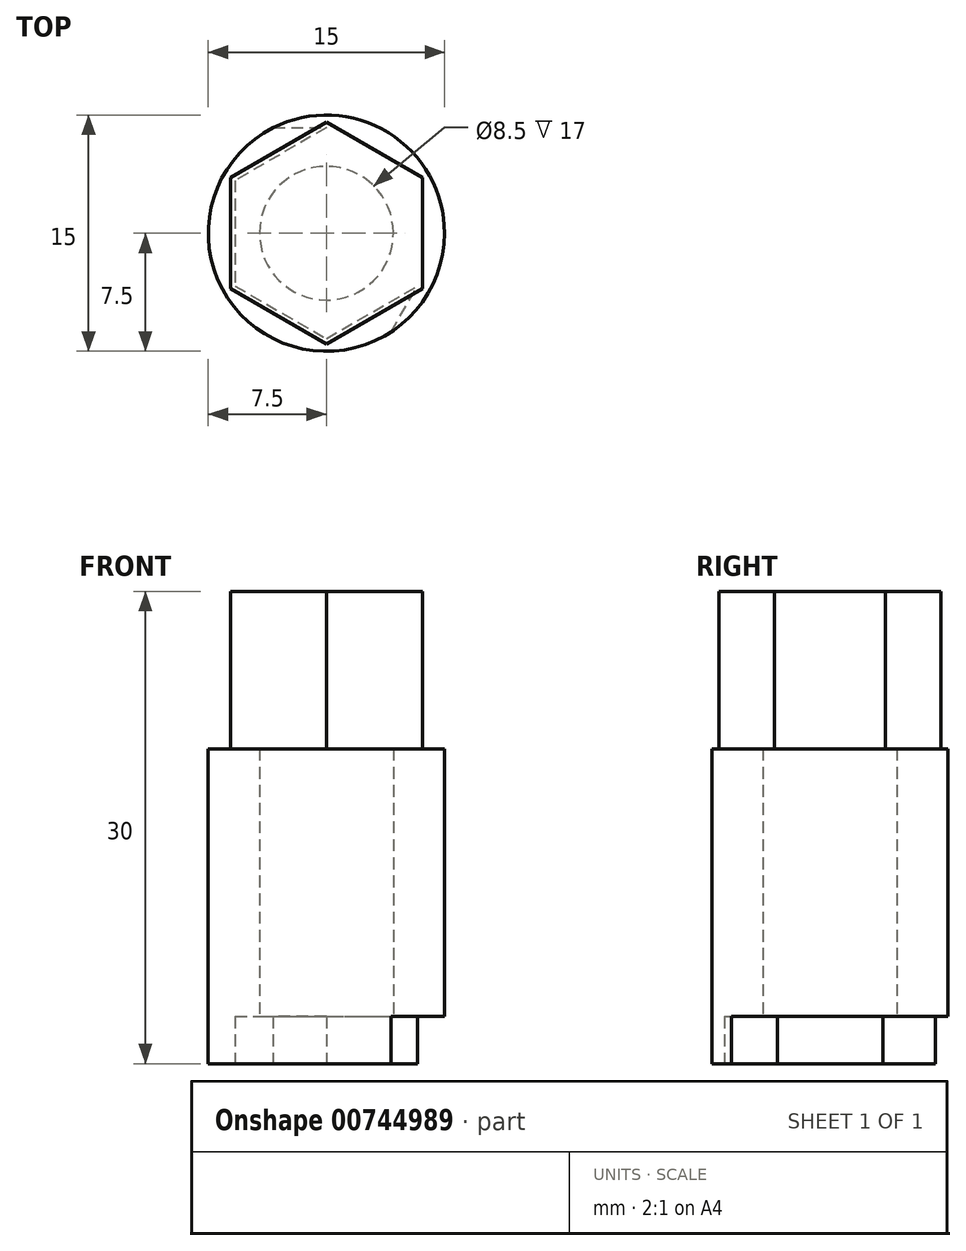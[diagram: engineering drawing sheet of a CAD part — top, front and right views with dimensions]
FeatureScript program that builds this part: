
annotation { "Feature Type Name" : "Feature", "Feature Type Description" : "" }
export const myFeature = defineFeature(function(context is Context, id is Id, definition is map)
    precondition{}
    {
        {
            var Q0;
            Q0=qCreatedBy(makeId("Top.planeOp"),FACE);
            var sketch = newSketch(context, id + "F0", { "sketchPlane" : qUnion([Q0])});
            skCircle(sketch, "E0", {"center": v(0, 0) * mm, "radius": 7.5 * mm});
            skSolve(sketch);
        }
        {
            var Q0;
            Q0=makeQuery(id+"F0.imprint","IMPRINT",FACE,{"disambiguationData":[TD([[makeQuery(id+"F0.imprint","IMPRINT",EDGE,{"derivedFrom":sQuery(id+"F0.wireOp",EDGE,"E0")}),1.0]])]});
            extrude(context, id + "F1", {"entities" : qUnion([Q0]), "depth" : 30 * mm, "offsetDistance" : 25 * mm});
        }
        {
            var Q0;
            Q0=makeQuery(id+"F1.opExtrude","CAP_FACE",FACE,{"disambiguationData":[OSD([sQuery(id+"F0.wireOp",EDGE,"E0")])],"isStart":true});
            var sketch = newSketch(context, id + "F2", { "sketchPlane" : qUnion([Q0])});
            skCircle(sketch, "E1", {"center": v(0, 0) * mm, "radius": 4.25 * mm});
            skSolve(sketch);
        }
        {
            var Q0;
            Q0=makeQuery(id+"F2.imprint","IMPRINT",FACE,{"disambiguationData":[TD([[makeQuery(id+"F2.imprint","IMPRINT",EDGE,{"derivedFrom":sQuery(id+"F2.wireOp",EDGE,"E1")}),1.0]])]});
            extrude(context, id + "F3", {"entities" : qUnion([Q0]), "operationType" : NewBodyOperationType.REMOVE, "oppositeDirection" : true, "depth" : 20 * mm, "offsetDistance" : 25 * mm});
        }
        {
            var Q0;
            Q0=makeQuery(id+"F1.opExtrude","CAP_FACE",FACE,{"disambiguationData":[OSD([sQuery(id+"F0.wireOp",EDGE,"E0")])],"isStart":true});
            var sketch = newSketch(context, id + "F4", { "sketchPlane" : qUnion([Q0])});
            skCircle(sketch, "E2.cCircle", {"center": v(0, 0) * mm, "radius": 5.8 * mm, "construction": true});
            skLineSegment(sketch, "E2.0", {"start": v(5.8, 3.35) * mm, "end": v(5.8, -3.35) * mm});
            skLineSegment(sketch, "E2.1", {"start": v(5.8, -3.35) * mm, "end": v(0, -6.7) * mm});
            skLineSegment(sketch, "E2.2", {"start": v(0, -6.7) * mm, "end": v(-5.8, -3.35) * mm});
            skLineSegment(sketch, "E2.3", {"start": v(-5.8, -3.35) * mm, "end": v(-5.8, 3.35) * mm});
            skLineSegment(sketch, "E2.4", {"start": v(-5.8, 3.35) * mm, "end": v(0, 6.7) * mm});
            skLineSegment(sketch, "E2.5", {"start": v(0, 6.7) * mm, "end": v(5.8, 3.35) * mm});
            skPoint(sketch, "E2.0.midPoint", {"position": v(5.8, 0) * mm});
            skSolve(sketch);
        }
        {
            var Q0;
            Q0=makeQuery(id+"F4.imprint","IMPRINT",FACE,{"disambiguationData":[TD([[makeQuery(id+"F4.imprint","IMPRINT",EDGE,{"derivedFrom":sQuery(id+"F4.wireOp",EDGE,"E2.0")}),-1.0]])]});
            extrude(context, id + "F5", {"entities" : qUnion([Q0]), "operationType" : NewBodyOperationType.REMOVE, "oppositeDirection" : true, "depth" : 3 * mm, "offsetDistance" : 25 * mm});
        }
        {
            var Q0;
            Q0=makeQuery(id+"F1.opExtrude","CAP_FACE",FACE,{"disambiguationData":[OSD([sQuery(id+"F0.wireOp",EDGE,"E0")])],"isStart":true});
            var sketch = newSketch(context, id + "F6", { "sketchPlane" : qUnion([Q0])});
            skCircle(sketch, "E3", {"center": v(0, 0) * mm, "radius": 6.5 * mm});
            skSolve(sketch);
        }
        {
            var Q0;
            Q0=makeQuery(id+"F1.opExtrude","CAP_FACE",FACE,{"disambiguationData":[OSD([sQuery(id+"F0.wireOp",EDGE,"E0")])],"isStart":false});
            var sketch = newSketch(context, id + "F7", { "sketchPlane" : qUnion([Q0])});
            skCircle(sketch, "E4.cCircle", {"center": v(0, 0) * mm, "radius": 6.1 * mm, "construction": true});
            skLineSegment(sketch, "E4.0", {"start": v(6.1, 3.52) * mm, "end": v(6.1, -3.52) * mm});
            skLineSegment(sketch, "E4.1", {"start": v(6.1, -3.52) * mm, "end": v(0, -7.04) * mm});
            skLineSegment(sketch, "E4.2", {"start": v(0, -7.04) * mm, "end": v(-6.1, -3.52) * mm});
            skLineSegment(sketch, "E4.3", {"start": v(-6.1, -3.52) * mm, "end": v(-6.1, 3.52) * mm});
            skLineSegment(sketch, "E4.4", {"start": v(-6.1, 3.52) * mm, "end": v(0, 7.04) * mm});
            skLineSegment(sketch, "E4.5", {"start": v(0, 7.04) * mm, "end": v(6.1, 3.52) * mm});
            skPoint(sketch, "E4.0.midPoint", {"position": v(6.1, 0) * mm});
            skSolve(sketch);
        }
        {
            var Q0;
            Q0=makeQuery(id+"F7.imprint","IMPRINT",FACE,{"disambiguationData":[TD([[makeQuery(id+"F7.imprint","IMPRINT",EDGE,{"derivedFrom":sQuery(id+"F7.wireOp",EDGE,"E4.0")}),1.0]])]});
            var Q1;
            {var subQ0=sQuery(id+"F7.wireOp",EDGE,"E4.5");var subQ1=makeQuery(id+"F1.opExtrude","CAP_EDGE",EDGE,{"disambiguationData":[OSD([sQuery(id+"F0.wireOp",EDGE,"E0")])],"isStart":false});var subQ2=makeQuery(id+"F7.imprint","INTERSECT",VERTEX,{"disambiguationData":[OD(0.0)],"derivedFrom":[subQ1,subQ0]});Q1=makeQuery(id+"F7.imprint","IMPRINT",FACE,{"disambiguationData":[TD([[makeQuery(id+"F7.imprint","IMPRINT",EDGE,{"disambiguationData":[TD([[subQ2,-1.0]])],"derivedFrom":subQ0}),1.0]])]});}
            var Q2;
            {var subQ0=sQuery(id+"F7.wireOp",EDGE,"E4.4");var subQ1=makeQuery(id+"F1.opExtrude","CAP_EDGE",EDGE,{"disambiguationData":[OSD([sQuery(id+"F0.wireOp",EDGE,"E0")])],"isStart":false});var subQ2=makeQuery(id+"F7.imprint","INTERSECT",VERTEX,{"disambiguationData":[OD(0.0)],"derivedFrom":[subQ1,subQ0]});Q2=makeQuery(id+"F7.imprint","IMPRINT",FACE,{"disambiguationData":[TD([[makeQuery(id+"F7.imprint","IMPRINT",EDGE,{"disambiguationData":[TD([[subQ2,-1.0]])],"derivedFrom":subQ0}),1.0]])]});}
            var Q3;
            {var subQ0=sQuery(id+"F7.wireOp",EDGE,"E4.3");var subQ1=makeQuery(id+"F1.opExtrude","CAP_EDGE",EDGE,{"disambiguationData":[OSD([sQuery(id+"F0.wireOp",EDGE,"E0")])],"isStart":false});var subQ2=makeQuery(id+"F7.imprint","INTERSECT",VERTEX,{"disambiguationData":[OD(0.0)],"derivedFrom":[subQ1,subQ0]});Q3=makeQuery(id+"F7.imprint","IMPRINT",FACE,{"disambiguationData":[TD([[makeQuery(id+"F7.imprint","IMPRINT",EDGE,{"disambiguationData":[TD([[subQ2,-1.0]])],"derivedFrom":subQ0}),1.0]])]});}
            var Q4;
            {var subQ0=sQuery(id+"F7.wireOp",EDGE,"E4.2");var subQ1=makeQuery(id+"F1.opExtrude","CAP_EDGE",EDGE,{"disambiguationData":[OSD([sQuery(id+"F0.wireOp",EDGE,"E0")])],"isStart":false});var subQ2=makeQuery(id+"F7.imprint","INTERSECT",VERTEX,{"disambiguationData":[OD(0.0)],"derivedFrom":[subQ1,subQ0]});Q4=makeQuery(id+"F7.imprint","IMPRINT",FACE,{"disambiguationData":[TD([[makeQuery(id+"F7.imprint","IMPRINT",EDGE,{"disambiguationData":[TD([[subQ2,-1.0]])],"derivedFrom":subQ0}),1.0]])]});}
            var Q5;
            {var subQ0=sQuery(id+"F7.wireOp",EDGE,"E4.1");var subQ1=makeQuery(id+"F1.opExtrude","CAP_EDGE",EDGE,{"disambiguationData":[OSD([sQuery(id+"F0.wireOp",EDGE,"E0")])],"isStart":false});var subQ2=makeQuery(id+"F7.imprint","INTERSECT",VERTEX,{"disambiguationData":[OD(0.0)],"derivedFrom":[subQ1,subQ0]});Q5=makeQuery(id+"F7.imprint","IMPRINT",FACE,{"disambiguationData":[TD([[makeQuery(id+"F7.imprint","IMPRINT",EDGE,{"disambiguationData":[TD([[subQ2,-1.0]])],"derivedFrom":subQ0}),1.0]])]});}
            extrude(context, id + "F8", {"entities" : qUnion([Q0, Q1, Q2, Q3, Q4, Q5]), "operationType" : NewBodyOperationType.REMOVE, "oppositeDirection" : true, "depth" : 10 * mm, "offsetDistance" : 25 * mm});
        }
        {
            var Q0;
            Q0=makeQuery(id+"F1.opExtrude","CAP_FACE",FACE,{"disambiguationData":[OSD([sQuery(id+"F0.wireOp",EDGE,"E0")])],"isStart":true});
            var sketch = newSketch(context, id + "F9", { "sketchPlane" : qUnion([Q0])});
            skLineSegment(sketch, "E5.0.0", {"start": v(5.8, 3.35) * mm, "end": v(0, 6.7) * mm});
            skLineSegment(sketch, "E5.0.1", {"start": v(0, 6.7) * mm, "end": v(-5.8, 3.35) * mm});
            skLineSegment(sketch, "E5.0.2", {"start": v(-5.8, 3.35) * mm, "end": v(-5.8, -3.35) * mm});
            skLineSegment(sketch, "E5.0.3", {"start": v(-5.8, -3.35) * mm, "end": v(0, -6.7) * mm});
            skLineSegment(sketch, "E5.0.4", {"start": v(0, -6.7) * mm, "end": v(5.8, -3.35) * mm});
            skLineSegment(sketch, "E5.0.5", {"start": v(5.8, -3.35) * mm, "end": v(5.8, 3.35) * mm});
            skCircle(sketch, "E6.0", {"center": v(0, 0) * mm, "radius": 4.25 * mm});
            skCircle(sketch, "E7.0", {"center": v(0, 0) * mm, "radius": 7.5 * mm});
            skLineSegment(sketch, "E8", {"start": v(4.11, 6.27) * mm, "end": v(5.8, 3.35) * mm});
            skPoint(sketch, "E9", {"position": v(5.8, 3.35) * mm});
            skLineSegment(sketch, "E10", {"start": v(-3.38, -6.7) * mm, "end": v(0, -6.7) * mm});
            skPoint(sketch, "E11", {"position": v(0, -6.7) * mm});
            skSolve(sketch);
        }
        {
            var Q0;
            Q0=makeQuery(id+"F9.imprint","IMPRINT",FACE,{"disambiguationData":[TD([[makeQuery(id+"F9.imprint","IMPRINT",EDGE,{"derivedFrom":sQuery(id+"F9.wireOp",EDGE,"E5.0.4")}),1.0]])]});
            var Q1;
            Q1=makeQuery(id+"F5.boolean.opBoolean","COPY",FACE,{"derivedFrom":makeQuery(id+"F5.opExtrude","CAP_FACE",FACE,{"disambiguationData":[OSD([sQuery(id+"F2.wireOp",EDGE,"E1"),sQuery(id+"F4.wireOp",EDGE,"E2.0"),sQuery(id+"F4.wireOp",EDGE,"E2.1"),sQuery(id+"F4.wireOp",EDGE,"E2.2"),sQuery(id+"F4.wireOp",EDGE,"E2.3"),sQuery(id+"F4.wireOp",EDGE,"E2.4"),sQuery(id+"F4.wireOp",EDGE,"E2.5")])],"isStart":false})});
            extrude(context, id + "F10", {"entities" : qUnion([Q0]), "operationType" : NewBodyOperationType.REMOVE, "endBound" : BoundingType.UP_TO_SURFACE, "oppositeDirection" : true, "depth" : 25 * mm, "endBoundEntityFace" : qUnion([Q1]), "offsetDistance" : 25 * mm});
        }
    });
